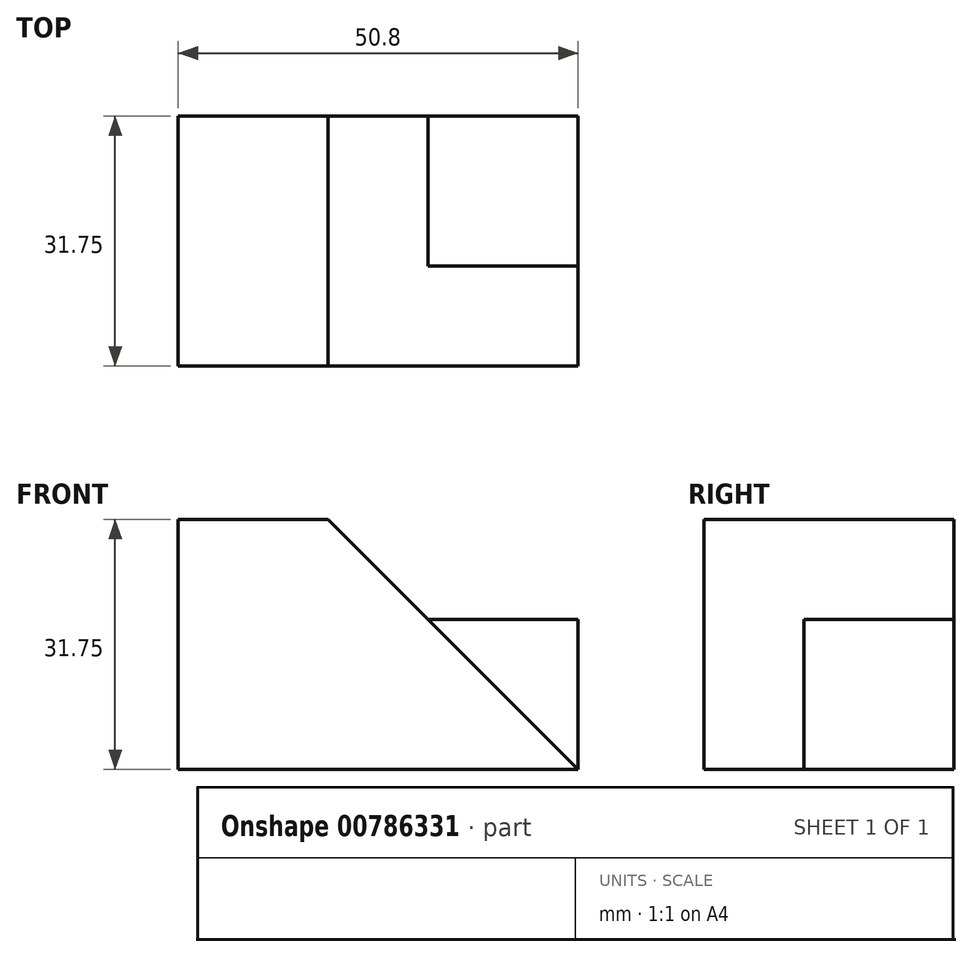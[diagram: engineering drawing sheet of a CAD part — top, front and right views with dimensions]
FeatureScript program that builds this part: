
annotation { "Feature Type Name" : "Feature", "Feature Type Description" : "" }
export const myFeature = defineFeature(function(context is Context, id is Id, definition is map)
    precondition{}
    {
        {
            var Q0;
            Q0=qCreatedBy(makeId("Front.planeOp"),FACE);
            var sketch = newSketch(context, id + "F0", { "sketchPlane" : qUnion([Q0])});
            skLineSegment(sketch, "E0", {"start": v(0, 0) * mm, "end": v(0, 31.75) * mm});
            skLineSegment(sketch, "E1", {"start": v(0, 31.75) * mm, "end": v(19.05, 31.75) * mm});
            skLineSegment(sketch, "E2", {"start": v(0, 0) * mm, "end": v(50.8, 0) * mm});
            skLineSegment(sketch, "E3", {"start": v(50.8, 0) * mm, "end": v(19.05, 31.75) * mm});
            skLineSegment(sketch, "E4", {"start": v(50.8, 0) * mm, "end": v(50.8, 19.05) * mm});
            skLineSegment(sketch, "E5", {"start": v(50.8, 19.05) * mm, "end": v(31.75, 19.05) * mm});
            skSolve(sketch);
        }
        {
            var Q0;
            Q0=makeQuery(id+"F0.imprint","IMPRINT",FACE,{"disambiguationData":[TD([[makeQuery(id+"F0.imprint","IMPRINT",EDGE,{"derivedFrom":sQuery(id+"F0.wireOp",EDGE,"E0")}),-1.0]])]});
            var Q1;
            {var subQ0=sQuery(id+"F0.wireOp",EDGE,"E4");Q1=makeQuery(id+"F0.imprint","IMPRINT",FACE,{"disambiguationData":[TD([[makeQuery(id+"F0.imprint","IMPRINT",EDGE,{"derivedFrom":subQ0}),1.0]])]});}
            extrude(context, id + "F1", {"entities" : qUnion([Q0, Q1]), "depth" : 25.4 * mm, "offsetDistance" : 25.4 * mm});
        }
        {
            var Q0;
            Q0=makeQuery(id+"F1.opExtrude","CAP_FACE",FACE,{"disambiguationData":[OSD([sQuery(id+"F0.wireOp",EDGE,"E0"),sQuery(id+"F0.wireOp",EDGE,"E1"),sQuery(id+"F0.wireOp",EDGE,"E2"),sQuery(id+"F0.wireOp",EDGE,"E3"),sQuery(id+"F0.wireOp",EDGE,"E4"),sQuery(id+"F0.wireOp",EDGE,"E5")])],"isStart":false});
            var sketch = newSketch(context, id + "F2", { "sketchPlane" : qUnion([Q0])});
            skLineSegment(sketch, "E6", {"start": v(31.75, 19.05) * mm, "end": v(50.8, 0) * mm});
            skSolve(sketch);
        }
        {
            var Q0;
            Q0=makeQuery(id+"F2.imprint","IMPRINT",FACE,{"disambiguationData":[TD([[makeQuery(id+"F2.imprint","IMPRINT",EDGE,{"derivedFrom":sQuery(id+"F2.wireOp",EDGE,"E6")}),1.0]])]});
            extrude(context, id + "F3", {"entities" : qUnion([Q0]), "operationType" : NewBodyOperationType.REMOVE, "oppositeDirection" : true, "depth" : 12.7 * mm, "offsetDistance" : 25.4 * mm});
        }
        {
            var Q0;
            Q0=makeQuery(id+"F1.opExtrude","CAP_FACE",FACE,{"disambiguationData":[OSD([sQuery(id+"F0.wireOp",EDGE,"E0"),sQuery(id+"F0.wireOp",EDGE,"E1"),sQuery(id+"F0.wireOp",EDGE,"E2"),sQuery(id+"F0.wireOp",EDGE,"E3"),sQuery(id+"F0.wireOp",EDGE,"E4"),sQuery(id+"F0.wireOp",EDGE,"E5")])],"isStart":true});
            extrude(context, id + "F4", {"entities" : qUnion([Q0]), "operationType" : NewBodyOperationType.ADD, "depth" : 6.35 * mm, "offsetDistance" : 25.4 * mm});
        }
    });
